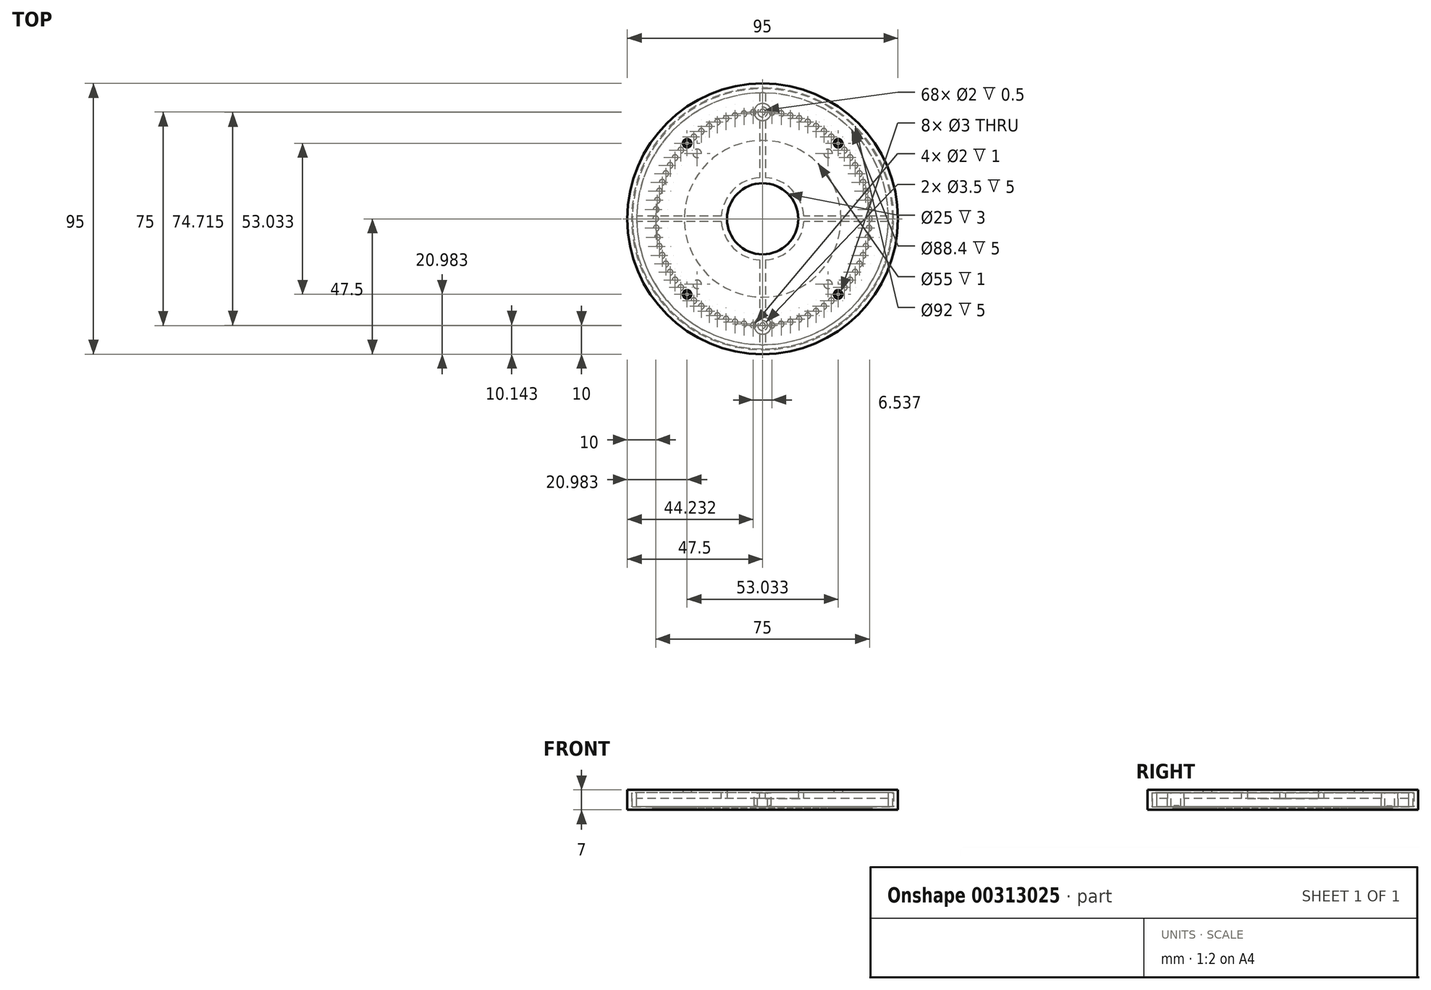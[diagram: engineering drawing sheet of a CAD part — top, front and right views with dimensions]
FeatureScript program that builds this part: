
annotation { "Feature Type Name" : "Feature", "Feature Type Description" : "" }
export const myFeature = defineFeature(function(context is Context, id is Id, definition is map)
    precondition{}
    {
        {
            var Q0;
            Q0=qCreatedBy(makeId("Top.planeOp"),FACE);
            var sketch = newSketch(context, id + "F0", { "sketchPlane" : qUnion([Q0])});
            skCircle(sketch, "E0", {"center": v(0, 0) * mm, "radius": 47.5 * mm});
            skCircle(sketch, "E1", {"center": v(0, 0) * mm, "radius": 27.5 * mm});
            skCircle(sketch, "E2", {"center": v(0, 0) * mm, "radius": 32.5 * mm, "construction": true});
            skCircle(sketch, "E3", {"center": v(-22.98, -22.98) * mm, "radius": 1.5 * mm});
            skLineSegment(sketch, "E4", {"start": v(-22.98, -22.98) * mm, "end": v(0, 0) * mm, "construction": true});
            skCircle(sketch, "E5.1.0", {"center": v(22.98, -22.98) * mm, "radius": 1.5 * mm});
            skCircle(sketch, "E5.2.0", {"center": v(22.98, 22.98) * mm, "radius": 1.5 * mm});
            skCircle(sketch, "E5.3.0", {"center": v(-22.98, 22.98) * mm, "radius": 1.5 * mm});
            skSolve(sketch);
        }
        {
            var Q0;
            Q0 = qSketchRegion(id + "F0", true);
            extrude(context, id + "F1", {"entities" : qUnion([Q0]), "depth" : 1 * mm});
        }
        {
            var Q0;
            Q0=makeQuery(id+"F1.opExtrude","CAP_FACE",FACE,{"disambiguationData":[OSD([sQuery(id+"F0.wireOp",EDGE,"E0"),sQuery(id+"F0.wireOp",EDGE,"E1")])],"isStart":false});
            var sketch = newSketch(context, id + "F2", { "sketchPlane" : qUnion([Q0])});
            skCircle(sketch, "E6", {"center": v(0, 0) * mm, "radius": 37.5 * mm, "construction": true});
            skCircle(sketch, "E7", {"center": v(0, 37.5) * mm, "radius": 1 * mm});
            skCircle(sketch, "E8.1.0", {"center": v(-3.27, 37.36) * mm, "radius": 1 * mm});
            skCircle(sketch, "E8.2.0", {"center": v(-6.51, 36.93) * mm, "radius": 1 * mm});
            skCircle(sketch, "E8.3.0", {"center": v(-9.7, 36.22) * mm, "radius": 1 * mm});
            skCircle(sketch, "E8.4.0", {"center": v(-12.83, 35.24) * mm, "radius": 1 * mm});
            skCircle(sketch, "E8.5.0", {"center": v(-15.85, 33.99) * mm, "radius": 1 * mm});
            skCircle(sketch, "E8.6.0", {"center": v(-18.75, 32.48) * mm, "radius": 1 * mm});
            skCircle(sketch, "E8.7.0", {"center": v(-21.5, 30.72) * mm, "radius": 1 * mm});
            skCircle(sketch, "E8.8.0", {"center": v(-24.1, 28.73) * mm, "radius": 1 * mm});
            skCircle(sketch, "E8.9.0", {"center": v(-26.52, 26.52) * mm, "radius": 1 * mm});
            skCircle(sketch, "E8.10.0", {"center": v(-28.73, 24.1) * mm, "radius": 1 * mm});
            skCircle(sketch, "E8.11.0", {"center": v(-30.72, 21.5) * mm, "radius": 1 * mm});
            skCircle(sketch, "E8.12.0", {"center": v(-32.48, 18.75) * mm, "radius": 1 * mm});
            skCircle(sketch, "E8.13.0", {"center": v(-33.99, 15.85) * mm, "radius": 1 * mm});
            skCircle(sketch, "E8.14.0", {"center": v(-35.24, 12.83) * mm, "radius": 1 * mm});
            skCircle(sketch, "E8.15.0", {"center": v(-36.22, 9.7) * mm, "radius": 1 * mm});
            skCircle(sketch, "E8.16.0", {"center": v(-36.93, 6.51) * mm, "radius": 1 * mm});
            skCircle(sketch, "E8.17.0", {"center": v(-37.36, 3.27) * mm, "radius": 1 * mm});
            skCircle(sketch, "E8.18.0", {"center": v(-37.5, 0) * mm, "radius": 1 * mm});
            skCircle(sketch, "E8.19.0", {"center": v(-37.36, -3.27) * mm, "radius": 1 * mm});
            skCircle(sketch, "E8.20.0", {"center": v(-36.93, -6.51) * mm, "radius": 1 * mm});
            skCircle(sketch, "E8.21.0", {"center": v(-36.22, -9.7) * mm, "radius": 1 * mm});
            skCircle(sketch, "E8.22.0", {"center": v(-35.24, -12.83) * mm, "radius": 1 * mm});
            skCircle(sketch, "E8.23.0", {"center": v(-33.99, -15.85) * mm, "radius": 1 * mm});
            skCircle(sketch, "E8.24.0", {"center": v(-32.48, -18.75) * mm, "radius": 1 * mm});
            skCircle(sketch, "E8.25.0", {"center": v(-30.72, -21.5) * mm, "radius": 1 * mm});
            skCircle(sketch, "E8.26.0", {"center": v(-28.73, -24.1) * mm, "radius": 1 * mm});
            skCircle(sketch, "E8.27.0", {"center": v(-26.52, -26.52) * mm, "radius": 1 * mm});
            skCircle(sketch, "E8.28.0", {"center": v(-24.1, -28.73) * mm, "radius": 1 * mm});
            skCircle(sketch, "E8.29.0", {"center": v(-21.5, -30.72) * mm, "radius": 1 * mm});
            skCircle(sketch, "E8.30.0", {"center": v(-18.75, -32.48) * mm, "radius": 1 * mm});
            skCircle(sketch, "E8.31.0", {"center": v(-15.85, -33.99) * mm, "radius": 1 * mm});
            skCircle(sketch, "E8.32.0", {"center": v(-12.83, -35.24) * mm, "radius": 1 * mm});
            skCircle(sketch, "E8.33.0", {"center": v(-9.7, -36.22) * mm, "radius": 1 * mm});
            skCircle(sketch, "E8.34.0", {"center": v(-6.51, -36.93) * mm, "radius": 1 * mm});
            skCircle(sketch, "E8.35.0", {"center": v(-3.27, -37.36) * mm, "radius": 1 * mm});
            skCircle(sketch, "E9.1.36.0", {"center": v(0, -37.5) * mm, "radius": 1 * mm});
            skCircle(sketch, "E9.1.37.0", {"center": v(3.27, -37.36) * mm, "radius": 1 * mm});
            skCircle(sketch, "E9.1.38.0", {"center": v(6.51, -36.93) * mm, "radius": 1 * mm});
            skCircle(sketch, "E9.1.39.0", {"center": v(9.7, -36.22) * mm, "radius": 1 * mm});
            skCircle(sketch, "E9.1.40.0", {"center": v(12.83, -35.24) * mm, "radius": 1 * mm});
            skCircle(sketch, "E9.1.41.0", {"center": v(15.85, -33.99) * mm, "radius": 1 * mm});
            skCircle(sketch, "E9.1.42.0", {"center": v(18.75, -32.48) * mm, "radius": 1 * mm});
            skCircle(sketch, "E9.1.43.0", {"center": v(21.5, -30.72) * mm, "radius": 1 * mm});
            skCircle(sketch, "E9.1.44.0", {"center": v(24.1, -28.73) * mm, "radius": 1 * mm});
            skCircle(sketch, "E9.1.45.0", {"center": v(26.52, -26.52) * mm, "radius": 1 * mm});
            skCircle(sketch, "E9.1.46.0", {"center": v(28.73, -24.1) * mm, "radius": 1 * mm});
            skCircle(sketch, "E9.1.47.0", {"center": v(30.72, -21.5) * mm, "radius": 1 * mm});
            skCircle(sketch, "E9.1.48.0", {"center": v(32.48, -18.75) * mm, "radius": 1 * mm});
            skCircle(sketch, "E9.1.49.0", {"center": v(33.99, -15.85) * mm, "radius": 1 * mm});
            skCircle(sketch, "E9.1.50.0", {"center": v(35.24, -12.83) * mm, "radius": 1 * mm});
            skCircle(sketch, "E9.1.51.0", {"center": v(36.22, -9.7) * mm, "radius": 1 * mm});
            skCircle(sketch, "E9.1.52.0", {"center": v(36.93, -6.51) * mm, "radius": 1 * mm});
            skCircle(sketch, "E9.1.53.0", {"center": v(37.36, -3.27) * mm, "radius": 1 * mm});
            skCircle(sketch, "E9.1.54.0", {"center": v(37.5, 0) * mm, "radius": 1 * mm});
            skCircle(sketch, "E9.1.55.0", {"center": v(37.36, 3.27) * mm, "radius": 1 * mm});
            skCircle(sketch, "E9.1.56.0", {"center": v(36.93, 6.51) * mm, "radius": 1 * mm});
            skCircle(sketch, "E9.1.57.0", {"center": v(36.22, 9.7) * mm, "radius": 1 * mm});
            skCircle(sketch, "E9.1.58.0", {"center": v(35.24, 12.83) * mm, "radius": 1 * mm});
            skCircle(sketch, "E9.1.59.0", {"center": v(33.99, 15.85) * mm, "radius": 1 * mm});
            skCircle(sketch, "E9.1.60.0", {"center": v(32.48, 18.75) * mm, "radius": 1 * mm});
            skCircle(sketch, "E9.1.61.0", {"center": v(30.72, 21.5) * mm, "radius": 1 * mm});
            skCircle(sketch, "E9.1.62.0", {"center": v(28.73, 24.1) * mm, "radius": 1 * mm});
            skCircle(sketch, "E9.1.63.0", {"center": v(26.52, 26.52) * mm, "radius": 1 * mm});
            skCircle(sketch, "E9.1.64.0", {"center": v(24.1, 28.73) * mm, "radius": 1 * mm});
            skCircle(sketch, "E9.1.65.0", {"center": v(21.5, 30.72) * mm, "radius": 1 * mm});
            skCircle(sketch, "E9.1.66.0", {"center": v(18.75, 32.48) * mm, "radius": 1 * mm});
            skCircle(sketch, "E9.1.67.0", {"center": v(15.85, 33.99) * mm, "radius": 1 * mm});
            skCircle(sketch, "E9.1.68.0", {"center": v(12.83, 35.24) * mm, "radius": 1 * mm});
            skCircle(sketch, "E9.1.69.0", {"center": v(9.7, 36.22) * mm, "radius": 1 * mm});
            skCircle(sketch, "E9.1.70.0", {"center": v(6.51, 36.93) * mm, "radius": 1 * mm});
            skCircle(sketch, "E9.1.71.0", {"center": v(3.27, 37.36) * mm, "radius": 1 * mm});
            skSolve(sketch);
        }
        {
            var Q0;
            Q0 = qSketchRegion(id + "F2", true);
            extrude(context, id + "F3", {"entities" : qUnion([Q0]), "operationType" : NewBodyOperationType.REMOVE, "oppositeDirection" : true, "depth" : 0.5 * mm});
        }
        {
            var Q0;
            Q0=makeQuery(id+"F1.opExtrude","CAP_FACE",FACE,{"disambiguationData":[OSD([sQuery(id+"F0.wireOp",EDGE,"E0"),sQuery(id+"F0.wireOp",EDGE,"E1")])],"isStart":false});
            var sketch = newSketch(context, id + "F4", { "sketchPlane" : qUnion([Q0])});
            skCircle(sketch, "E10", {"center": v(0, 0) * mm, "radius": 46 * mm});
            skCircle(sketch, "E11", {"center": v(0, 0) * mm, "radius": 47.5 * mm});
            skSolve(sketch);
        }
        {
            var Q0;
            Q0 = qSketchRegion(id + "F4", true);
            extrude(context, id + "F5", {"entities" : qUnion([Q0]), "operationType" : NewBodyOperationType.ADD, "depth" : 5 * mm});
        }
        {
            var Q0;
            Q0=makeQuery(id+"F5.opExtrude","CAP_FACE",FACE,{"disambiguationData":[OSD([sQuery(id+"F4.wireOp",EDGE,"E10"),sQuery(id+"F4.wireOp",EDGE,"E11")])],"isStart":false});
            var sketch = newSketch(context, id + "F6", { "sketchPlane" : qUnion([Q0])});
            skCircle(sketch, "E12", {"center": v(0, 0) * mm, "radius": 12.5 * mm});
            skCircle(sketch, "E13", {"center": v(0, 0) * mm, "radius": 47.5 * mm});
            skCircle(sketch, "E14", {"center": v(0, 0) * mm, "radius": 37.5 * mm, "construction": true});
            skCircle(sketch, "E15", {"center": v(-26.52, -26.52) * mm, "radius": 1.5 * mm});
            skLineSegment(sketch, "E16", {"start": v(-26.52, -26.52) * mm, "end": v(0, 0) * mm, "construction": true});
            skCircle(sketch, "E17.1.0", {"center": v(26.52, -26.52) * mm, "radius": 1.5 * mm});
            skCircle(sketch, "E17.2.0", {"center": v(26.52, 26.52) * mm, "radius": 1.5 * mm});
            skCircle(sketch, "E17.3.0", {"center": v(-26.52, 26.52) * mm, "radius": 1.5 * mm});
            skSolve(sketch);
        }
        {
            var Q0;
            Q0 = qSketchRegion(id + "F6", true);
            extrude(context, id + "F7", {"entities" : qUnion([Q0]), "depth" : 1 * mm});
        }
        {
            var Q0;
            Q0=makeQuery(id+"F7.opExtrude","CAP_FACE",FACE,{"disambiguationData":[OSD([sQuery(id+"F6.wireOp",EDGE,"E12"),sQuery(id+"F6.wireOp",EDGE,"E13")])],"isStart":true});
            var sketch = newSketch(context, id + "F8", { "sketchPlane" : qUnion([Q0])});
            skCircle(sketch, "E18", {"center": v(0, 37.5) * mm, "radius": 1.75 * mm});
            skCircle(sketch, "E19", {"center": v(0, 37.5) * mm, "radius": 3 * mm});
            skCircle(sketch, "E20", {"center": v(0, 0) * mm, "radius": 45.7 * mm});
            skCircle(sketch, "E21", {"center": v(0, 0) * mm, "radius": 44.2 * mm});
            skCircle(sketch, "E22.1.0", {"center": v(0, -37.5) * mm, "radius": 1.75 * mm});
            skCircle(sketch, "E22.1.1", {"center": v(0, -37.5) * mm, "radius": 3 * mm});
            skSolve(sketch);
        }
        {
            var Q0;
            Q0 = qSketchRegion(id + "F8", true);
            var Q1;
            Q1=makeQuery(id+"F8.imprint","IMPRINT",FACE,{"disambiguationData":[TD([[makeQuery(id+"F8.imprint","IMPRINT",EDGE,{"derivedFrom":sQuery(id+"F8.wireOp",EDGE,"E22.1.0")}),-1.0]])]});
            var Q2;
            Q2=makeQuery(id+"F8.imprint","IMPRINT",FACE,{"disambiguationData":[TD([[makeQuery(id+"F8.imprint","IMPRINT",EDGE,{"derivedFrom":sQuery(id+"F8.wireOp",EDGE,"E18")}),-1.0]])]});
            extrude(context, id + "F9", {"entities" : qUnion([Q0, Q1, Q2]), "operationType" : NewBodyOperationType.ADD, "depth" : 5 * mm});
        }
        {
            var Q0;
            Q0=makeQuery(id+"F9.opExtrude","CAP_FACE",FACE,{"disambiguationData":[OSD([sQuery(id+"F8.wireOp",EDGE,"E18"),sQuery(id+"F8.wireOp",EDGE,"E19")])],"isStart":false});
            var Q1;
            Q1=makeQuery(id+"F9.opExtrude","CAP_FACE",FACE,{"disambiguationData":[OSD([sQuery(id+"F8.wireOp",EDGE,"E22.1.0"),sQuery(id+"F8.wireOp",EDGE,"E22.1.1")])],"isStart":false});
            extrude(context, id + "F10", {"entities" : qUnion([Q0, Q1]), "operationType" : NewBodyOperationType.REMOVE, "oppositeDirection" : true, "depth" : 0.5 * mm});
        }
        {
            var Q0;
            {var subQ0=sQuery(id+"F6.wireOp",EDGE,"E12");Q0=makeQuery(id+"F9.boolean.opBoolean","SPLIT",FACE,{"disambiguationData":[TD([makeQuery(id+"F7.opExtrude","SWEPT_FACE",FACE,{"disambiguationData":[OSD([subQ0])]})])],"derivedFrom":makeQuery(id+"F7.opExtrude","CAP_FACE",FACE,{"disambiguationData":[OSD([subQ0,sQuery(id+"F6.wireOp",EDGE,"E13")])],"isStart":true})});}
            var sketch = newSketch(context, id + "F11", { "sketchPlane" : qUnion([Q0])});
            skArc(sketch, "E23", {"start": v(-14.47, -1) * mm, "mid": v(-10.25, -10.25) * mm, "end": v(-1, -14.47) * mm});
            skLineSegment(sketch, "E24.bottom", {"start": v(1, -45.5) * mm, "end": v(-1, -45.5) * mm});
            skLineSegment(sketch, "E24.top", {"start": v(1, 45.5) * mm, "end": v(-1, 45.5) * mm});
            skLineSegment(sketch, "E24.left", {"start": v(1, -45.5) * mm, "end": v(1, -14.47) * mm});
            skLineSegment(sketch, "E24.right", {"start": v(-1, -45.5) * mm, "end": v(-1, -14.47) * mm});
            skLineSegment(sketch, "E25.bottom", {"start": v(45.1, -1) * mm, "end": v(14.47, -1) * mm});
            skLineSegment(sketch, "E25.top", {"start": v(45.1, 1) * mm, "end": v(14.47, 1) * mm});
            skLineSegment(sketch, "E25.left", {"start": v(45.1, -1) * mm, "end": v(45.1, 1) * mm});
            skLineSegment(sketch, "E25.right", {"start": v(-45.1, -1) * mm, "end": v(-45.1, 1) * mm});
            skLineSegment(sketch, "E26.trimOffspring", {"start": v(-14.47, 1) * mm, "end": v(-45.1, 1) * mm});
            skLineSegment(sketch, "E27.trimOffspring", {"start": v(-14.47, -1) * mm, "end": v(-45.1, -1) * mm});
            skLineSegment(sketch, "E28.trimOffspring", {"start": v(1, 14.47) * mm, "end": v(1, 45.5) * mm});
            skLineSegment(sketch, "E29.trimOffspring", {"start": v(-1, 14.47) * mm, "end": v(-1, 45.5) * mm});
            skArc(sketch, "E30.trimOffspring", {"start": v(1, -14.47) * mm, "mid": v(10.25, -10.25) * mm, "end": v(14.47, -1) * mm});
            skArc(sketch, "E31.trimOffspring", {"start": v(14.47, 1) * mm, "mid": v(10.25, 10.25) * mm, "end": v(1, 14.47) * mm});
            skArc(sketch, "E32.trimOffspring", {"start": v(-1, 14.47) * mm, "mid": v(-10.25, 10.25) * mm, "end": v(-14.47, 1) * mm});
            skSolve(sketch);
        }
        {
            var Q0;
            {var subQ5=sQuery(id+"F11.wireOp",EDGE,"E23");Q0=makeQuery(id+"F11.imprint","IMPRINT",FACE,{"disambiguationData":[TD([[makeQuery(id+"F11.imprint","IMPRINT",EDGE,{"derivedFrom":subQ5}),1.0]])]});}
            var Q1;
            {var subQ0=sQuery(id+"F11.wireOp",EDGE,"E24.left");var subQ1=makeQuery(id+"F9.opExtrude","CAP_EDGE",EDGE,{"disambiguationData":[OSD([sQuery(id+"F8.wireOp",EDGE,"E21")])],"isStart":true});var subQ2=makeQuery(id+"F11.imprint","INTERSECT",VERTEX,{"derivedFrom":[subQ1,subQ0]});Q1=makeQuery(id+"F11.imprint","IMPRINT",FACE,{"disambiguationData":[TD([[makeQuery(id+"F11.imprint","IMPRINT",EDGE,{"disambiguationData":[TD([[subQ2,-1.0]])],"derivedFrom":subQ0}),1.0]])]});}
            var Q2;
            {var subQ0=sQuery(id+"F11.wireOp",EDGE,"E28.trimOffspring");var subQ1=makeQuery(id+"F9.opExtrude","CAP_EDGE",EDGE,{"disambiguationData":[OSD([sQuery(id+"F8.wireOp",EDGE,"E21")])],"isStart":true});var subQ2=makeQuery(id+"F11.imprint","INTERSECT",VERTEX,{"derivedFrom":[subQ1,subQ0]});Q2=makeQuery(id+"F11.imprint","IMPRINT",FACE,{"disambiguationData":[TD([[makeQuery(id+"F11.imprint","IMPRINT",EDGE,{"disambiguationData":[TD([[subQ2,1.0]])],"derivedFrom":subQ0}),1.0]])]});}
            extrude(context, id + "F12", {"entities" : qUnion([Q0, Q1, Q2]), "operationType" : NewBodyOperationType.ADD, "depth" : 2 * mm});
        }
    });
